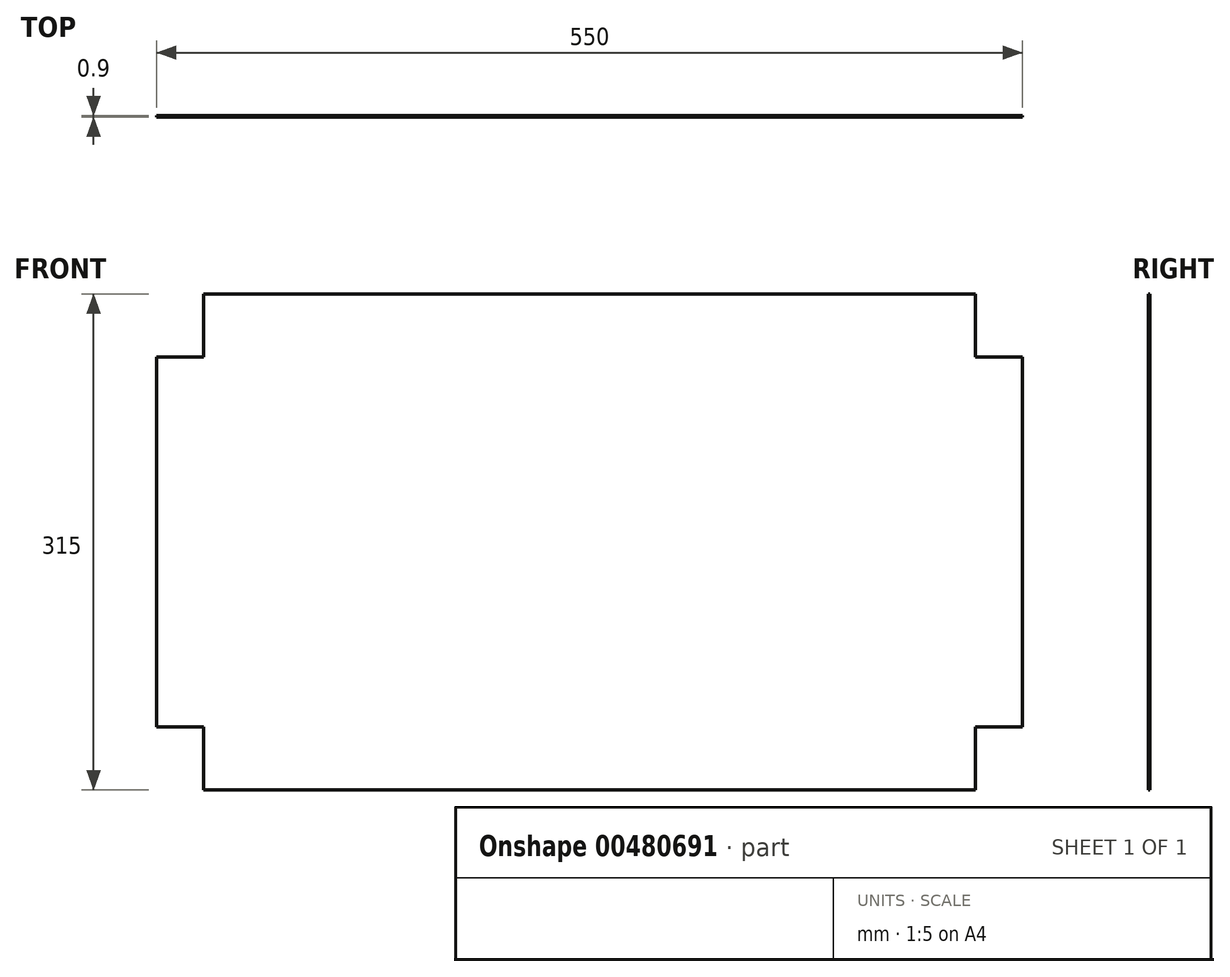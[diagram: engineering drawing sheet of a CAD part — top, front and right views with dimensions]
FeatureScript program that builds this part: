
annotation { "Feature Type Name" : "Feature", "Feature Type Description" : "" }
export const myFeature = defineFeature(function(context is Context, id is Id, definition is map)
    precondition{}
    {
        {
            var Q0;
            Q0=qCreatedBy(makeId("Front.planeOp"),FACE);
            var sketch = newSketch(context, id + "F0", { "sketchPlane" : qUnion([Q0])});
            skLineSegment(sketch, "E0", {"start": v(-311.34, 5.17) * mm, "end": v(178.66, 5.17) * mm});
            skLineSegment(sketch, "E1", {"start": v(178.66, 5.17) * mm, "end": v(178.66, -34.83) * mm});
            skLineSegment(sketch, "E2", {"start": v(178.66, -34.83) * mm, "end": v(208.66, -34.83) * mm});
            skLineSegment(sketch, "E3", {"start": v(-311.34, 5.17) * mm, "end": v(-311.34, -34.83) * mm});
            skLineSegment(sketch, "E4", {"start": v(-311.34, -34.83) * mm, "end": v(-341.34, -34.83) * mm});
            skLineSegment(sketch, "E5", {"start": v(208.66, -34.83) * mm, "end": v(208.66, -269.83) * mm});
            skLineSegment(sketch, "E6", {"start": v(-341.34, -34.83) * mm, "end": v(-341.34, -269.83) * mm});
            skLineSegment(sketch, "E7", {"start": v(-341.34, -269.83) * mm, "end": v(-311.34, -269.83) * mm});
            skLineSegment(sketch, "E8", {"start": v(-311.34, -269.83) * mm, "end": v(-311.34, -309.83) * mm});
            skLineSegment(sketch, "E9", {"start": v(208.66, -269.83) * mm, "end": v(178.66, -269.83) * mm});
            skLineSegment(sketch, "E10", {"start": v(178.66, -269.83) * mm, "end": v(178.66, -309.83) * mm});
            skLineSegment(sketch, "E11", {"start": v(-311.34, -309.83) * mm, "end": v(178.66, -309.83) * mm});
            skSolve(sketch);
        }
        {
            var Q0;
            Q0=makeQuery(id+"F0.imprint","IMPRINT",FACE,{"disambiguationData":[TD([[makeQuery(id+"F0.imprint","IMPRINT",EDGE,{"derivedFrom":sQuery(id+"F0.wireOp",EDGE,"E0")}),-1.0]])]});
            extrude(context, id + "F1", {"entities" : qUnion([Q0]), "depth" : 0.9 * mm});
        }
    });
